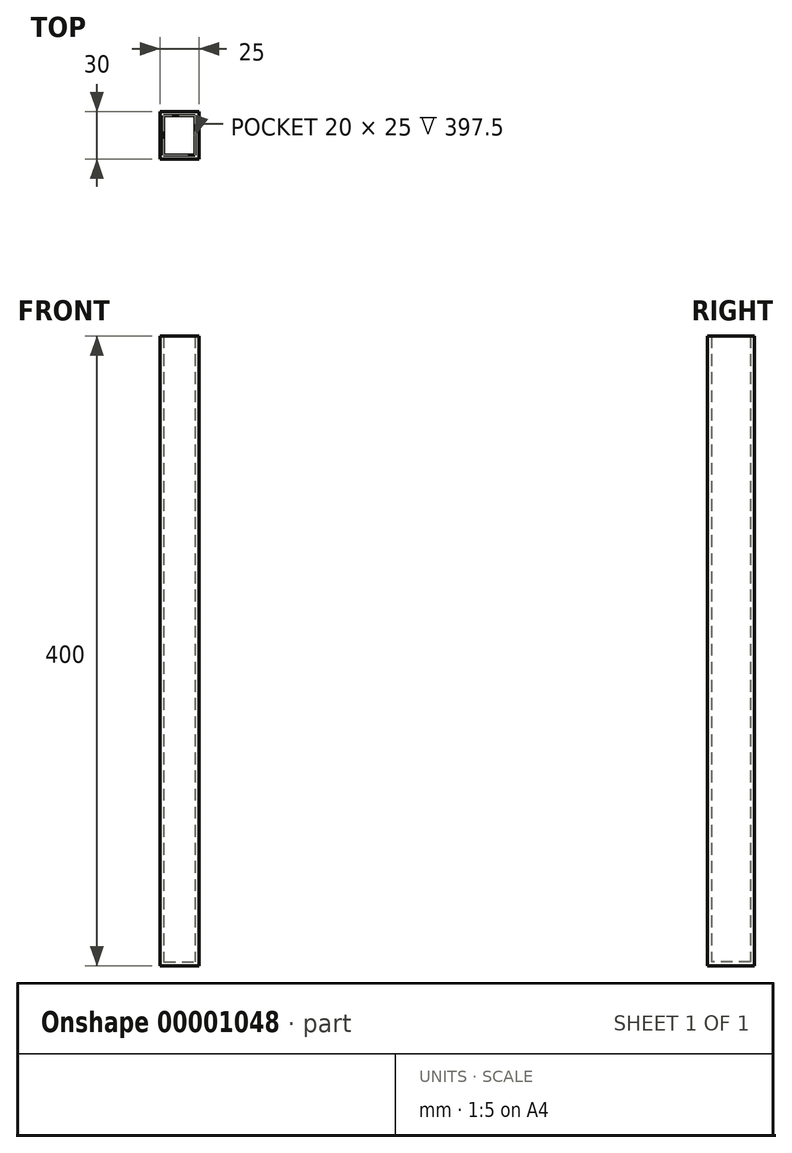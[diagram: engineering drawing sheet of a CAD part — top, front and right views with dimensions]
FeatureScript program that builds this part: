
annotation { "Feature Type Name" : "Feature", "Feature Type Description" : "" }
export const myFeature = defineFeature(function(context is Context, id is Id, definition is map)
    precondition{}
    {
        {
            var Q0;
            Q0=qCreatedBy(makeId("Top.planeOp"),FACE);
            var sketch = newSketch(context, id + "F0", { "sketchPlane" : qUnion([Q0])});
            skLineSegment(sketch, "E0", {"start": v(-61.3, -30.04) * mm, "end": v(-61.3, -60.04) * mm});
            skLineSegment(sketch, "E1", {"start": v(-61.3, -60.04) * mm, "end": v(-36.3, -60.04) * mm});
            skLineSegment(sketch, "E2", {"start": v(-36.3, -60.04) * mm, "end": v(-36.3, -30.04) * mm});
            skSolve(sketch);
        }
        {
            var Q0;
            Q0=sQuery(id+"F0.wireOp",EDGE,"E0");
            var Q1;
            Q1=sQuery(id+"F0.wireOp",EDGE,"E1");
            var Q2;
            Q2=sQuery(id+"F0.wireOp",EDGE,"E2");
            extrude(context, id + "F1", {"bodyType" : ToolBodyType.SURFACE, "surfaceEntities" : qUnion([Q0, Q1, Q2]), "depth" : 25 * mm, "offsetDistance" : 25 * mm});
        }
        {
            var Q0;
            Q0=qCreatedBy(makeId("Top.planeOp"),FACE);
            var sketch = newSketch(context, id + "F2", { "sketchPlane" : qUnion([Q0])});
            skLineSegment(sketch, "E3.bottom", {"start": v(32.1, -32.32) * mm, "end": v(57.1, -32.32) * mm});
            skLineSegment(sketch, "E3.top", {"start": v(32.1, -62.32) * mm, "end": v(57.1, -62.32) * mm});
            skLineSegment(sketch, "E3.left", {"start": v(32.1, -32.32) * mm, "end": v(32.1, -62.32) * mm});
            skLineSegment(sketch, "E3.right", {"start": v(57.1, -32.32) * mm, "end": v(57.1, -62.32) * mm});
            skSolve(sketch);
        }
        {
            var Q0;
            Q0=makeQuery(id+"F2.imprint","IMPRINT",FACE,{"disambiguationData":[TD([[makeQuery(id+"F2.imprint","IMPRINT",EDGE,{"derivedFrom":sQuery(id+"F2.wireOp",EDGE,"E3.bottom")}),-1.0]])]});
            extrude(context, id + "F3", {"entities" : qUnion([Q0]), "depth" : 400 * mm, "offsetDistance" : 25 * mm});
        }
        {
            var Q0;
            Q0=makeQuery(id+"F3.opExtrude","CAP_FACE",FACE,{"disambiguationData":[OSD([sQuery(id+"F2.wireOp",EDGE,"E3.bottom"),sQuery(id+"F2.wireOp",EDGE,"E3.top"),sQuery(id+"F2.wireOp",EDGE,"E3.left"),sQuery(id+"F2.wireOp",EDGE,"E3.right")])],"isStart":false});
            shell(context, id + "F4", {"entities" : qUnion([Q0]), "thickness" : 2.5 * mm});
        }
    });
